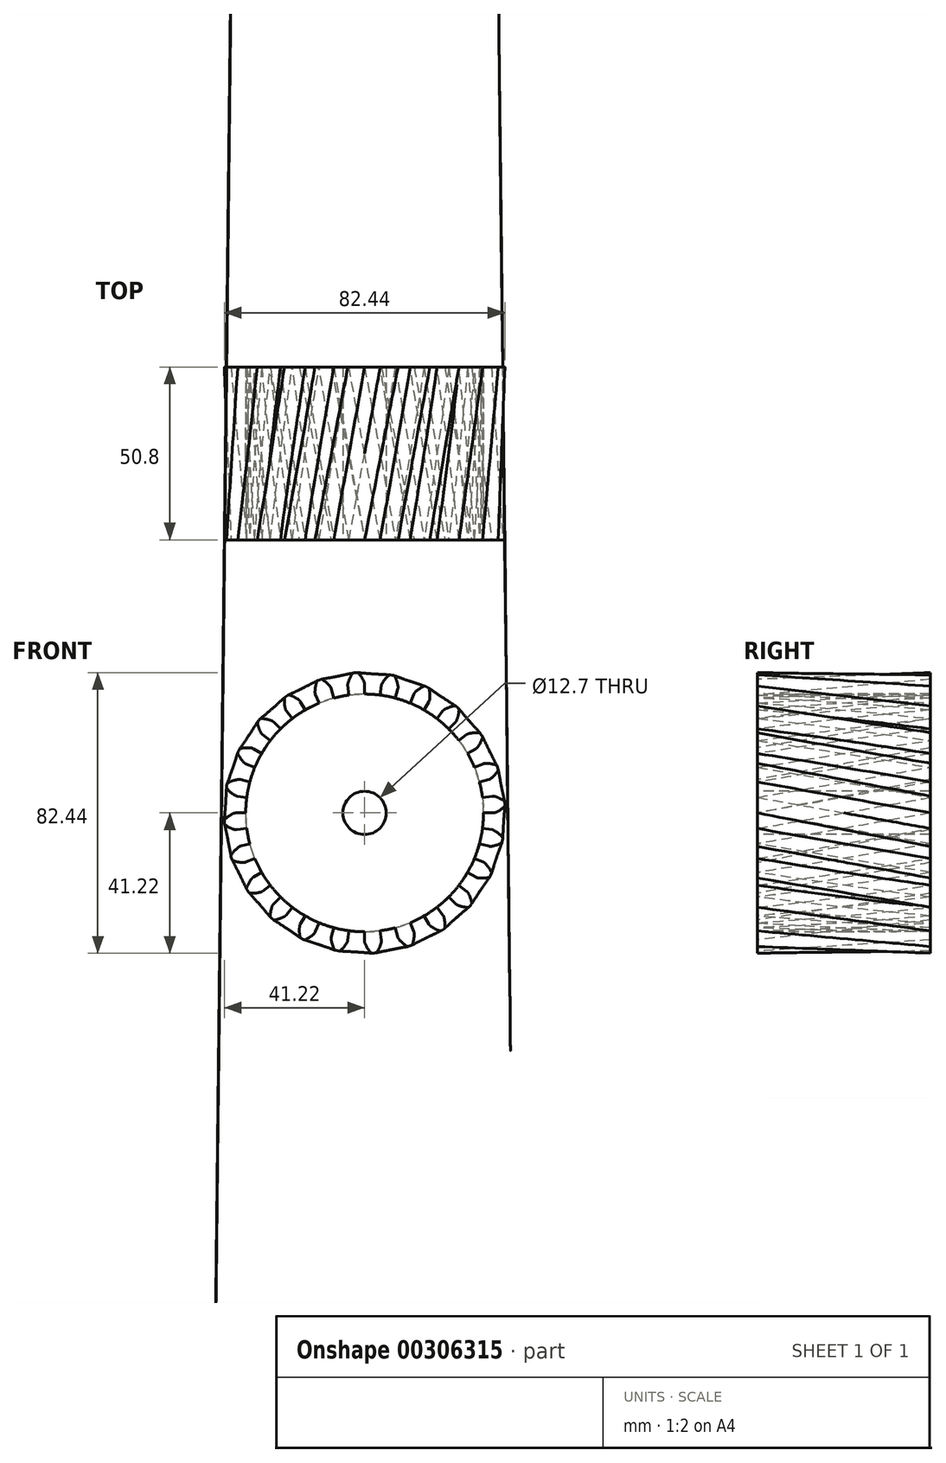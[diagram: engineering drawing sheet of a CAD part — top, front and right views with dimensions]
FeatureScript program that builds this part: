
annotation { "Feature Type Name" : "Feature", "Feature Type Description" : "" }
export const myFeature = defineFeature(function(context is Context, id is Id, definition is map)
    precondition{}
    {
        {
            var Q0;
            Q0=qCreatedBy(makeId("Front.planeOp"),FACE);
            var sketch = newSketch(context, id + "F0", { "sketchPlane" : qUnion([Q0])});
            skCircle(sketch, "E0", {"center": v(0, 0) * mm, "radius": 34.93 * mm});
            skArc(sketch, "E1.trimOffspring", {"start": v(-0.13, 38.41) * mm, "mid": v(-0.86, 39.8) * mm, "end": v(-1.8, 41.05) * mm});
            skLineSegment(sketch, "E2", {"start": v(0, 37.8) * mm, "end": v(0, 34.93) * mm});
            skLineSegment(sketch, "E3", {"start": v(-2.2, 41.22) * mm, "end": v(-2.7, 41.2) * mm});
            skArc(sketch, "E4.MirrorCS", {"start": v(-4.89, 38.1) * mm, "mid": v(-4.34, 39.57) * mm, "end": v(-3.57, 40.93) * mm});
            skLineSegment(sketch, "E5.MirrorCS", {"start": v(-4.93, 37.47) * mm, "end": v(-4.56, 34.63) * mm});
            skLineSegment(sketch, "E6.MirrorCS", {"start": v(-3.2, 41.15) * mm, "end": v(-2.7, 41.2) * mm});
            skPoint(sketch, "E7.visualSharp", {"position": v(-4.97, 37.77) * mm});
            skArc(sketch, "E7.filletArc", {"start": v(-4.89, 38.1) * mm, "mid": v(-4.94, 37.79) * mm, "end": v(-4.93, 37.47) * mm});
            skPoint(sketch, "E8.visualSharp", {"position": v(0, 38.1) * mm});
            skArc(sketch, "E8.filletArc", {"start": v(0, 37.8) * mm, "mid": v(-0.03, 38.1) * mm, "end": v(-0.13, 38.41) * mm});
            skPoint(sketch, "E9.visualSharp", {"position": v(-3.43, 41.13) * mm});
            skArc(sketch, "E9.filletArc", {"start": v(-3.2, 41.15) * mm, "mid": v(-3.4, 41.09) * mm, "end": v(-3.57, 40.93) * mm});
            skPoint(sketch, "E10.visualSharp", {"position": v(-1.97, 41.23) * mm});
            skArc(sketch, "E10.filletArc", {"start": v(-1.8, 41.05) * mm, "mid": v(-1.99, 41.18) * mm, "end": v(-2.2, 41.22) * mm});
            skLineSegment(sketch, "E11.1.0", {"start": v(-14.46, 34.91) * mm, "end": v(-13.37, 32.27) * mm});
            skArc(sketch, "E11.1.1", {"start": v(-14.58, 35.54) * mm, "mid": v(-14.55, 35.22) * mm, "end": v(-14.46, 34.91) * mm});
            skArc(sketch, "E11.1.2", {"start": v(-14.58, 35.54) * mm, "mid": v(-14.44, 37.1) * mm, "end": v(-14.04, 38.62) * mm});
            skLineSegment(sketch, "E11.1.3", {"start": v(-13.73, 38.92) * mm, "end": v(-13.27, 39.1) * mm});
            skLineSegment(sketch, "E11.1.4", {"start": v(-12.8, 39.24) * mm, "end": v(-13.27, 39.1) * mm});
            skArc(sketch, "E11.1.5", {"start": v(-12.37, 39.18) * mm, "mid": v(-12.58, 39.26) * mm, "end": v(-12.8, 39.24) * mm});
            skArc(sketch, "E11.1.6", {"start": v(-10.06, 37.07) * mm, "mid": v(-11.13, 38.22) * mm, "end": v(-12.37, 39.18) * mm});
            skArc(sketch, "E11.1.7", {"start": v(-13.73, 38.92) * mm, "mid": v(-13.92, 38.8) * mm, "end": v(-14.04, 38.62) * mm});
            skArc(sketch, "E11.1.8", {"start": v(-9.78, 36.5) * mm, "mid": v(-9.9, 36.8) * mm, "end": v(-10.06, 37.07) * mm});
            skLineSegment(sketch, "E11.1.9", {"start": v(-9.78, 36.5) * mm, "end": v(-9.04, 33.73) * mm});
            skLineSegment(sketch, "E11.2.0", {"start": v(-23, 29.98) * mm, "end": v(-21.26, 27.7) * mm});
            skArc(sketch, "E11.2.1", {"start": v(-23.28, 30.55) * mm, "mid": v(-23.17, 30.25) * mm, "end": v(-23, 29.98) * mm});
            skArc(sketch, "E11.2.2", {"start": v(-23.28, 30.55) * mm, "mid": v(-23.55, 32.1) * mm, "end": v(-23.56, 33.67) * mm});
            skLineSegment(sketch, "E11.2.3", {"start": v(-23.34, 34.04) * mm, "end": v(-22.93, 34.32) * mm});
            skLineSegment(sketch, "E11.2.4", {"start": v(-22.52, 34.6) * mm, "end": v(-22.93, 34.32) * mm});
            skArc(sketch, "E11.2.5", {"start": v(-22.09, 34.65) * mm, "mid": v(-22.31, 34.67) * mm, "end": v(-22.52, 34.6) * mm});
            skArc(sketch, "E11.2.6", {"start": v(-19.32, 33.2) * mm, "mid": v(-20.64, 34.04) * mm, "end": v(-22.09, 34.65) * mm});
            skArc(sketch, "E11.2.7", {"start": v(-23.34, 34.04) * mm, "mid": v(-23.49, 33.88) * mm, "end": v(-23.56, 33.67) * mm});
            skArc(sketch, "E11.2.8", {"start": v(-18.9, 32.73) * mm, "mid": v(-19.08, 32.99) * mm, "end": v(-19.32, 33.2) * mm});
            skLineSegment(sketch, "E11.2.9", {"start": v(-18.9, 32.73) * mm, "end": v(-17.46, 30.25) * mm});
            skLineSegment(sketch, "E11.3.0", {"start": v(-29.98, 23) * mm, "end": v(-27.7, 21.26) * mm});
            skArc(sketch, "E11.3.1", {"start": v(-30.4, 23.49) * mm, "mid": v(-30.21, 23.22) * mm, "end": v(-29.98, 23) * mm});
            skArc(sketch, "E11.3.2", {"start": v(-30.4, 23.49) * mm, "mid": v(-31.05, 24.9) * mm, "end": v(-31.47, 26.42) * mm});
            skLineSegment(sketch, "E11.3.3", {"start": v(-31.35, 26.84) * mm, "end": v(-31.04, 27.22) * mm});
            skLineSegment(sketch, "E11.3.4", {"start": v(-30.7, 27.58) * mm, "end": v(-31.04, 27.22) * mm});
            skArc(sketch, "E11.3.5", {"start": v(-30.3, 27.75) * mm, "mid": v(-30.52, 27.71) * mm, "end": v(-30.7, 27.58) * mm});
            skArc(sketch, "E11.3.6", {"start": v(-27.25, 27.07) * mm, "mid": v(-28.75, 27.54) * mm, "end": v(-30.3, 27.75) * mm});
            skArc(sketch, "E11.3.7", {"start": v(-31.35, 26.84) * mm, "mid": v(-31.46, 26.65) * mm, "end": v(-31.47, 26.42) * mm});
            skArc(sketch, "E11.3.8", {"start": v(-26.72, 26.72) * mm, "mid": v(-26.97, 26.92) * mm, "end": v(-27.25, 27.07) * mm});
            skLineSegment(sketch, "E11.3.9", {"start": v(-26.72, 26.72) * mm, "end": v(-24.7, 24.7) * mm});
            skLineSegment(sketch, "E11.4.0", {"start": v(-34.91, 14.46) * mm, "end": v(-32.27, 13.37) * mm});
            skArc(sketch, "E11.4.1", {"start": v(-35.44, 14.82) * mm, "mid": v(-35.2, 14.61) * mm, "end": v(-34.91, 14.46) * mm});
            skArc(sketch, "E11.4.2", {"start": v(-35.44, 14.82) * mm, "mid": v(-36.44, 16.02) * mm, "end": v(-37.23, 17.38) * mm});
            skLineSegment(sketch, "E11.4.3", {"start": v(-37.23, 17.81) * mm, "end": v(-37.02, 18.26) * mm});
            skLineSegment(sketch, "E11.4.4", {"start": v(-36.8, 18.7) * mm, "end": v(-37.02, 18.26) * mm});
            skArc(sketch, "E11.4.5", {"start": v(-36.45, 18.96) * mm, "mid": v(-36.66, 18.87) * mm, "end": v(-36.8, 18.7) * mm});
            skArc(sketch, "E11.4.6", {"start": v(-33.33, 19.1) * mm, "mid": v(-34.9, 19.16) * mm, "end": v(-36.45, 18.96) * mm});
            skArc(sketch, "E11.4.7", {"start": v(-37.23, 17.81) * mm, "mid": v(-37.28, 17.6) * mm, "end": v(-37.23, 17.38) * mm});
            skArc(sketch, "E11.4.8", {"start": v(-32.73, 18.9) * mm, "mid": v(-33.02, 19.03) * mm, "end": v(-33.33, 19.1) * mm});
            skLineSegment(sketch, "E11.4.9", {"start": v(-32.73, 18.9) * mm, "end": v(-30.25, 17.46) * mm});
            skLineSegment(sketch, "E11.5.0", {"start": v(-37.47, 4.93) * mm, "end": v(-34.63, 4.56) * mm});
            skArc(sketch, "E11.5.1", {"start": v(-38.07, 5.14) * mm, "mid": v(-37.78, 5) * mm, "end": v(-37.47, 4.93) * mm});
            skArc(sketch, "E11.5.2", {"start": v(-38.07, 5.14) * mm, "mid": v(-39.35, 6.05) * mm, "end": v(-40.46, 7.15) * mm});
            skLineSegment(sketch, "E11.5.3", {"start": v(-40.58, 7.57) * mm, "end": v(-40.49, 8.05) * mm});
            skLineSegment(sketch, "E11.5.4", {"start": v(-40.38, 8.53) * mm, "end": v(-40.49, 8.05) * mm});
            skArc(sketch, "E11.5.5", {"start": v(-40.12, 8.88) * mm, "mid": v(-40.29, 8.74) * mm, "end": v(-40.38, 8.53) * mm});
            skArc(sketch, "E11.5.6", {"start": v(-37.14, 9.82) * mm, "mid": v(-38.67, 9.47) * mm, "end": v(-40.12, 8.88) * mm});
            skArc(sketch, "E11.5.7", {"start": v(-40.58, 7.57) * mm, "mid": v(-40.57, 7.35) * mm, "end": v(-40.46, 7.15) * mm});
            skArc(sketch, "E11.5.8", {"start": v(-36.5, 9.78) * mm, "mid": v(-36.82, 9.83) * mm, "end": v(-37.14, 9.82) * mm});
            skLineSegment(sketch, "E11.5.9", {"start": v(-36.5, 9.78) * mm, "end": v(-33.73, 9.04) * mm});
            skLineSegment(sketch, "E11.6.0", {"start": v(-37.47, -4.93) * mm, "end": v(-34.63, -4.56) * mm});
            skArc(sketch, "E11.6.1", {"start": v(-38.1, -4.89) * mm, "mid": v(-37.79, -4.94) * mm, "end": v(-37.47, -4.93) * mm});
            skArc(sketch, "E11.6.2", {"start": v(-38.1, -4.89) * mm, "mid": v(-39.57, -4.34) * mm, "end": v(-40.93, -3.57) * mm});
            skLineSegment(sketch, "E11.6.3", {"start": v(-41.15, -3.2) * mm, "end": v(-41.2, -2.7) * mm});
            skLineSegment(sketch, "E11.6.4", {"start": v(-41.22, -2.2) * mm, "end": v(-41.2, -2.7) * mm});
            skArc(sketch, "E11.6.5", {"start": v(-41.05, -1.8) * mm, "mid": v(-41.18, -1.99) * mm, "end": v(-41.22, -2.2) * mm});
            skArc(sketch, "E11.6.6", {"start": v(-38.41, -0.13) * mm, "mid": v(-39.8, -0.86) * mm, "end": v(-41.05, -1.8) * mm});
            skArc(sketch, "E11.6.7", {"start": v(-41.15, -3.2) * mm, "mid": v(-41.09, -3.4) * mm, "end": v(-40.93, -3.57) * mm});
            skArc(sketch, "E11.6.8", {"start": v(-37.8, 0) * mm, "mid": v(-38.1, -0.03) * mm, "end": v(-38.41, -0.13) * mm});
            skLineSegment(sketch, "E11.6.9", {"start": v(-37.8, 0) * mm, "end": v(-34.93, 0) * mm});
            skLineSegment(sketch, "E11.7.0", {"start": v(-34.91, -14.46) * mm, "end": v(-32.27, -13.37) * mm});
            skArc(sketch, "E11.7.1", {"start": v(-35.54, -14.58) * mm, "mid": v(-35.22, -14.55) * mm, "end": v(-34.91, -14.46) * mm});
            skArc(sketch, "E11.7.2", {"start": v(-35.54, -14.58) * mm, "mid": v(-37.1, -14.44) * mm, "end": v(-38.62, -14.04) * mm});
            skLineSegment(sketch, "E11.7.3", {"start": v(-38.92, -13.73) * mm, "end": v(-39.1, -13.27) * mm});
            skLineSegment(sketch, "E11.7.4", {"start": v(-39.24, -12.8) * mm, "end": v(-39.1, -13.27) * mm});
            skArc(sketch, "E11.7.5", {"start": v(-39.18, -12.37) * mm, "mid": v(-39.26, -12.58) * mm, "end": v(-39.24, -12.8) * mm});
            skArc(sketch, "E11.7.6", {"start": v(-37.07, -10.06) * mm, "mid": v(-38.22, -11.13) * mm, "end": v(-39.18, -12.37) * mm});
            skArc(sketch, "E11.7.7", {"start": v(-38.92, -13.73) * mm, "mid": v(-38.8, -13.92) * mm, "end": v(-38.62, -14.04) * mm});
            skArc(sketch, "E11.7.8", {"start": v(-36.5, -9.78) * mm, "mid": v(-36.8, -9.9) * mm, "end": v(-37.07, -10.06) * mm});
            skLineSegment(sketch, "E11.7.9", {"start": v(-36.5, -9.78) * mm, "end": v(-33.73, -9.04) * mm});
            skLineSegment(sketch, "E11.8.0", {"start": v(-29.98, -23) * mm, "end": v(-27.7, -21.26) * mm});
            skArc(sketch, "E11.8.1", {"start": v(-30.55, -23.28) * mm, "mid": v(-30.25, -23.17) * mm, "end": v(-29.98, -23) * mm});
            skArc(sketch, "E11.8.2", {"start": v(-30.55, -23.28) * mm, "mid": v(-32.1, -23.55) * mm, "end": v(-33.67, -23.56) * mm});
            skLineSegment(sketch, "E11.8.3", {"start": v(-34.04, -23.34) * mm, "end": v(-34.32, -22.93) * mm});
            skLineSegment(sketch, "E11.8.4", {"start": v(-34.6, -22.52) * mm, "end": v(-34.32, -22.93) * mm});
            skArc(sketch, "E11.8.5", {"start": v(-34.65, -22.09) * mm, "mid": v(-34.67, -22.31) * mm, "end": v(-34.6, -22.52) * mm});
            skArc(sketch, "E11.8.6", {"start": v(-33.2, -19.32) * mm, "mid": v(-34.04, -20.64) * mm, "end": v(-34.65, -22.09) * mm});
            skArc(sketch, "E11.8.7", {"start": v(-34.04, -23.34) * mm, "mid": v(-33.88, -23.49) * mm, "end": v(-33.67, -23.56) * mm});
            skArc(sketch, "E11.8.8", {"start": v(-32.73, -18.9) * mm, "mid": v(-32.99, -19.08) * mm, "end": v(-33.2, -19.32) * mm});
            skLineSegment(sketch, "E11.8.9", {"start": v(-32.73, -18.9) * mm, "end": v(-30.25, -17.46) * mm});
            skLineSegment(sketch, "E11.9.0", {"start": v(-23, -29.98) * mm, "end": v(-21.26, -27.7) * mm});
            skArc(sketch, "E11.9.1", {"start": v(-23.49, -30.4) * mm, "mid": v(-23.22, -30.21) * mm, "end": v(-23, -29.98) * mm});
            skArc(sketch, "E11.9.2", {"start": v(-23.49, -30.4) * mm, "mid": v(-24.9, -31.05) * mm, "end": v(-26.42, -31.47) * mm});
            skLineSegment(sketch, "E11.9.3", {"start": v(-26.84, -31.35) * mm, "end": v(-27.22, -31.04) * mm});
            skLineSegment(sketch, "E11.9.4", {"start": v(-27.58, -30.7) * mm, "end": v(-27.22, -31.04) * mm});
            skArc(sketch, "E11.9.5", {"start": v(-27.75, -30.3) * mm, "mid": v(-27.71, -30.52) * mm, "end": v(-27.58, -30.7) * mm});
            skArc(sketch, "E11.9.6", {"start": v(-27.07, -27.25) * mm, "mid": v(-27.54, -28.75) * mm, "end": v(-27.75, -30.3) * mm});
            skArc(sketch, "E11.9.7", {"start": v(-26.84, -31.35) * mm, "mid": v(-26.65, -31.46) * mm, "end": v(-26.42, -31.47) * mm});
            skArc(sketch, "E11.9.8", {"start": v(-26.72, -26.72) * mm, "mid": v(-26.92, -26.97) * mm, "end": v(-27.07, -27.25) * mm});
            skLineSegment(sketch, "E11.9.9", {"start": v(-26.72, -26.72) * mm, "end": v(-24.7, -24.7) * mm});
            skLineSegment(sketch, "E11.10.0", {"start": v(-14.46, -34.91) * mm, "end": v(-13.37, -32.27) * mm});
            skArc(sketch, "E11.10.1", {"start": v(-14.82, -35.44) * mm, "mid": v(-14.61, -35.2) * mm, "end": v(-14.46, -34.91) * mm});
            skArc(sketch, "E11.10.2", {"start": v(-14.82, -35.44) * mm, "mid": v(-16.02, -36.44) * mm, "end": v(-17.38, -37.23) * mm});
            skLineSegment(sketch, "E11.10.3", {"start": v(-17.81, -37.23) * mm, "end": v(-18.26, -37.02) * mm});
            skLineSegment(sketch, "E11.10.4", {"start": v(-18.7, -36.8) * mm, "end": v(-18.26, -37.02) * mm});
            skArc(sketch, "E11.10.5", {"start": v(-18.96, -36.45) * mm, "mid": v(-18.87, -36.66) * mm, "end": v(-18.7, -36.8) * mm});
            skArc(sketch, "E11.10.6", {"start": v(-19.1, -33.33) * mm, "mid": v(-19.16, -34.9) * mm, "end": v(-18.96, -36.45) * mm});
            skArc(sketch, "E11.10.7", {"start": v(-17.81, -37.23) * mm, "mid": v(-17.6, -37.28) * mm, "end": v(-17.38, -37.23) * mm});
            skArc(sketch, "E11.10.8", {"start": v(-18.9, -32.73) * mm, "mid": v(-19.03, -33.02) * mm, "end": v(-19.1, -33.33) * mm});
            skLineSegment(sketch, "E11.10.9", {"start": v(-18.9, -32.73) * mm, "end": v(-17.46, -30.25) * mm});
            skLineSegment(sketch, "E11.11.0", {"start": v(-4.93, -37.47) * mm, "end": v(-4.56, -34.63) * mm});
            skArc(sketch, "E11.11.1", {"start": v(-5.14, -38.07) * mm, "mid": v(-5, -37.78) * mm, "end": v(-4.93, -37.47) * mm});
            skArc(sketch, "E11.11.2", {"start": v(-5.14, -38.07) * mm, "mid": v(-6.05, -39.35) * mm, "end": v(-7.15, -40.46) * mm});
            skLineSegment(sketch, "E11.11.3", {"start": v(-7.57, -40.58) * mm, "end": v(-8.05, -40.49) * mm});
            skLineSegment(sketch, "E11.11.4", {"start": v(-8.53, -40.38) * mm, "end": v(-8.05, -40.49) * mm});
            skArc(sketch, "E11.11.5", {"start": v(-8.88, -40.12) * mm, "mid": v(-8.74, -40.29) * mm, "end": v(-8.53, -40.38) * mm});
            skArc(sketch, "E11.11.6", {"start": v(-9.82, -37.14) * mm, "mid": v(-9.47, -38.67) * mm, "end": v(-8.88, -40.12) * mm});
            skArc(sketch, "E11.11.7", {"start": v(-7.57, -40.58) * mm, "mid": v(-7.35, -40.57) * mm, "end": v(-7.15, -40.46) * mm});
            skArc(sketch, "E11.11.8", {"start": v(-9.78, -36.5) * mm, "mid": v(-9.83, -36.82) * mm, "end": v(-9.82, -37.14) * mm});
            skLineSegment(sketch, "E11.11.9", {"start": v(-9.78, -36.5) * mm, "end": v(-9.04, -33.73) * mm});
            skLineSegment(sketch, "E11.12.0", {"start": v(4.93, -37.47) * mm, "end": v(4.56, -34.63) * mm});
            skArc(sketch, "E11.12.1", {"start": v(4.89, -38.1) * mm, "mid": v(4.94, -37.79) * mm, "end": v(4.93, -37.47) * mm});
            skArc(sketch, "E11.12.2", {"start": v(4.89, -38.1) * mm, "mid": v(4.34, -39.57) * mm, "end": v(3.57, -40.93) * mm});
            skLineSegment(sketch, "E11.12.3", {"start": v(3.2, -41.15) * mm, "end": v(2.7, -41.2) * mm});
            skLineSegment(sketch, "E11.12.4", {"start": v(2.2, -41.22) * mm, "end": v(2.7, -41.2) * mm});
            skArc(sketch, "E11.12.5", {"start": v(1.8, -41.05) * mm, "mid": v(1.99, -41.18) * mm, "end": v(2.2, -41.22) * mm});
            skArc(sketch, "E11.12.6", {"start": v(0.13, -38.41) * mm, "mid": v(0.86, -39.8) * mm, "end": v(1.8, -41.05) * mm});
            skArc(sketch, "E11.12.7", {"start": v(3.2, -41.15) * mm, "mid": v(3.4, -41.09) * mm, "end": v(3.57, -40.93) * mm});
            skArc(sketch, "E11.12.8", {"start": v(0, -37.8) * mm, "mid": v(0.03, -38.1) * mm, "end": v(0.13, -38.41) * mm});
            skLineSegment(sketch, "E11.12.9", {"start": v(0, -37.8) * mm, "end": v(0, -34.93) * mm});
            skLineSegment(sketch, "E11.13.0", {"start": v(14.46, -34.91) * mm, "end": v(13.37, -32.27) * mm});
            skArc(sketch, "E11.13.1", {"start": v(14.58, -35.54) * mm, "mid": v(14.55, -35.22) * mm, "end": v(14.46, -34.91) * mm});
            skArc(sketch, "E11.13.2", {"start": v(14.58, -35.54) * mm, "mid": v(14.44, -37.1) * mm, "end": v(14.04, -38.62) * mm});
            skLineSegment(sketch, "E11.13.3", {"start": v(13.73, -38.92) * mm, "end": v(13.27, -39.1) * mm});
            skLineSegment(sketch, "E11.13.4", {"start": v(12.8, -39.24) * mm, "end": v(13.27, -39.1) * mm});
            skArc(sketch, "E11.13.5", {"start": v(12.37, -39.18) * mm, "mid": v(12.58, -39.26) * mm, "end": v(12.8, -39.24) * mm});
            skArc(sketch, "E11.13.6", {"start": v(10.06, -37.07) * mm, "mid": v(11.13, -38.22) * mm, "end": v(12.37, -39.18) * mm});
            skArc(sketch, "E11.13.7", {"start": v(13.73, -38.92) * mm, "mid": v(13.92, -38.8) * mm, "end": v(14.04, -38.62) * mm});
            skArc(sketch, "E11.13.8", {"start": v(9.78, -36.5) * mm, "mid": v(9.9, -36.8) * mm, "end": v(10.06, -37.07) * mm});
            skLineSegment(sketch, "E11.13.9", {"start": v(9.78, -36.5) * mm, "end": v(9.04, -33.73) * mm});
            skLineSegment(sketch, "E11.14.0", {"start": v(23, -29.98) * mm, "end": v(21.26, -27.7) * mm});
            skArc(sketch, "E11.14.1", {"start": v(23.28, -30.55) * mm, "mid": v(23.17, -30.25) * mm, "end": v(23, -29.98) * mm});
            skArc(sketch, "E11.14.2", {"start": v(23.28, -30.55) * mm, "mid": v(23.55, -32.1) * mm, "end": v(23.56, -33.67) * mm});
            skLineSegment(sketch, "E11.14.3", {"start": v(23.34, -34.04) * mm, "end": v(22.93, -34.32) * mm});
            skLineSegment(sketch, "E11.14.4", {"start": v(22.52, -34.6) * mm, "end": v(22.93, -34.32) * mm});
            skArc(sketch, "E11.14.5", {"start": v(22.09, -34.65) * mm, "mid": v(22.31, -34.67) * mm, "end": v(22.52, -34.6) * mm});
            skArc(sketch, "E11.14.6", {"start": v(19.32, -33.2) * mm, "mid": v(20.64, -34.04) * mm, "end": v(22.09, -34.65) * mm});
            skArc(sketch, "E11.14.7", {"start": v(23.34, -34.04) * mm, "mid": v(23.49, -33.88) * mm, "end": v(23.56, -33.67) * mm});
            skArc(sketch, "E11.14.8", {"start": v(18.9, -32.73) * mm, "mid": v(19.08, -32.99) * mm, "end": v(19.32, -33.2) * mm});
            skLineSegment(sketch, "E11.14.9", {"start": v(18.9, -32.73) * mm, "end": v(17.46, -30.25) * mm});
            skLineSegment(sketch, "E11.15.0", {"start": v(29.98, -23) * mm, "end": v(27.7, -21.26) * mm});
            skArc(sketch, "E11.15.1", {"start": v(30.4, -23.49) * mm, "mid": v(30.21, -23.22) * mm, "end": v(29.98, -23) * mm});
            skArc(sketch, "E11.15.2", {"start": v(30.4, -23.49) * mm, "mid": v(31.05, -24.9) * mm, "end": v(31.47, -26.42) * mm});
            skLineSegment(sketch, "E11.15.3", {"start": v(31.35, -26.84) * mm, "end": v(31.04, -27.22) * mm});
            skLineSegment(sketch, "E11.15.4", {"start": v(30.7, -27.58) * mm, "end": v(31.04, -27.22) * mm});
            skArc(sketch, "E11.15.5", {"start": v(30.3, -27.75) * mm, "mid": v(30.52, -27.71) * mm, "end": v(30.7, -27.58) * mm});
            skArc(sketch, "E11.15.6", {"start": v(27.25, -27.07) * mm, "mid": v(28.75, -27.54) * mm, "end": v(30.3, -27.75) * mm});
            skArc(sketch, "E11.15.7", {"start": v(31.35, -26.84) * mm, "mid": v(31.46, -26.65) * mm, "end": v(31.47, -26.42) * mm});
            skArc(sketch, "E11.15.8", {"start": v(26.72, -26.72) * mm, "mid": v(26.97, -26.92) * mm, "end": v(27.25, -27.07) * mm});
            skLineSegment(sketch, "E11.15.9", {"start": v(26.72, -26.72) * mm, "end": v(24.7, -24.7) * mm});
            skLineSegment(sketch, "E11.16.0", {"start": v(34.91, -14.46) * mm, "end": v(32.27, -13.37) * mm});
            skArc(sketch, "E11.16.1", {"start": v(35.44, -14.82) * mm, "mid": v(35.2, -14.61) * mm, "end": v(34.91, -14.46) * mm});
            skArc(sketch, "E11.16.2", {"start": v(35.44, -14.82) * mm, "mid": v(36.44, -16.02) * mm, "end": v(37.23, -17.38) * mm});
            skLineSegment(sketch, "E11.16.3", {"start": v(37.23, -17.81) * mm, "end": v(37.02, -18.26) * mm});
            skLineSegment(sketch, "E11.16.4", {"start": v(36.8, -18.7) * mm, "end": v(37.02, -18.26) * mm});
            skArc(sketch, "E11.16.5", {"start": v(36.45, -18.96) * mm, "mid": v(36.66, -18.87) * mm, "end": v(36.8, -18.7) * mm});
            skArc(sketch, "E11.16.6", {"start": v(33.33, -19.1) * mm, "mid": v(34.9, -19.16) * mm, "end": v(36.45, -18.96) * mm});
            skArc(sketch, "E11.16.7", {"start": v(37.23, -17.81) * mm, "mid": v(37.28, -17.6) * mm, "end": v(37.23, -17.38) * mm});
            skArc(sketch, "E11.16.8", {"start": v(32.73, -18.9) * mm, "mid": v(33.02, -19.03) * mm, "end": v(33.33, -19.1) * mm});
            skLineSegment(sketch, "E11.16.9", {"start": v(32.73, -18.9) * mm, "end": v(30.25, -17.46) * mm});
            skLineSegment(sketch, "E11.17.0", {"start": v(37.47, -4.93) * mm, "end": v(34.63, -4.56) * mm});
            skArc(sketch, "E11.17.1", {"start": v(38.07, -5.14) * mm, "mid": v(37.78, -5) * mm, "end": v(37.47, -4.93) * mm});
            skArc(sketch, "E11.17.2", {"start": v(38.07, -5.14) * mm, "mid": v(39.35, -6.05) * mm, "end": v(40.46, -7.15) * mm});
            skLineSegment(sketch, "E11.17.3", {"start": v(40.58, -7.57) * mm, "end": v(40.49, -8.05) * mm});
            skLineSegment(sketch, "E11.17.4", {"start": v(40.38, -8.53) * mm, "end": v(40.49, -8.05) * mm});
            skArc(sketch, "E11.17.5", {"start": v(40.12, -8.88) * mm, "mid": v(40.29, -8.74) * mm, "end": v(40.38, -8.53) * mm});
            skArc(sketch, "E11.17.6", {"start": v(37.14, -9.82) * mm, "mid": v(38.67, -9.47) * mm, "end": v(40.12, -8.88) * mm});
            skArc(sketch, "E11.17.7", {"start": v(40.58, -7.57) * mm, "mid": v(40.57, -7.35) * mm, "end": v(40.46, -7.15) * mm});
            skArc(sketch, "E11.17.8", {"start": v(36.5, -9.78) * mm, "mid": v(36.82, -9.83) * mm, "end": v(37.14, -9.82) * mm});
            skLineSegment(sketch, "E11.17.9", {"start": v(36.5, -9.78) * mm, "end": v(33.73, -9.04) * mm});
            skLineSegment(sketch, "E11.18.0", {"start": v(37.47, 4.93) * mm, "end": v(34.63, 4.56) * mm});
            skArc(sketch, "E11.18.1", {"start": v(38.1, 4.89) * mm, "mid": v(37.79, 4.94) * mm, "end": v(37.47, 4.93) * mm});
            skArc(sketch, "E11.18.2", {"start": v(38.1, 4.89) * mm, "mid": v(39.57, 4.34) * mm, "end": v(40.93, 3.57) * mm});
            skLineSegment(sketch, "E11.18.3", {"start": v(41.15, 3.2) * mm, "end": v(41.2, 2.7) * mm});
            skLineSegment(sketch, "E11.18.4", {"start": v(41.22, 2.2) * mm, "end": v(41.2, 2.7) * mm});
            skArc(sketch, "E11.18.5", {"start": v(41.05, 1.8) * mm, "mid": v(41.18, 1.99) * mm, "end": v(41.22, 2.2) * mm});
            skArc(sketch, "E11.18.6", {"start": v(38.41, 0.13) * mm, "mid": v(39.8, 0.86) * mm, "end": v(41.05, 1.8) * mm});
            skArc(sketch, "E11.18.7", {"start": v(41.15, 3.2) * mm, "mid": v(41.09, 3.4) * mm, "end": v(40.93, 3.57) * mm});
            skArc(sketch, "E11.18.8", {"start": v(37.8, 0) * mm, "mid": v(38.1, 0.03) * mm, "end": v(38.41, 0.13) * mm});
            skLineSegment(sketch, "E11.18.9", {"start": v(37.8, 0) * mm, "end": v(34.93, 0) * mm});
            skLineSegment(sketch, "E11.19.0", {"start": v(34.91, 14.46) * mm, "end": v(32.27, 13.37) * mm});
            skArc(sketch, "E11.19.1", {"start": v(35.54, 14.58) * mm, "mid": v(35.22, 14.55) * mm, "end": v(34.91, 14.46) * mm});
            skArc(sketch, "E11.19.2", {"start": v(35.54, 14.58) * mm, "mid": v(37.1, 14.44) * mm, "end": v(38.62, 14.04) * mm});
            skLineSegment(sketch, "E11.19.3", {"start": v(38.92, 13.73) * mm, "end": v(39.1, 13.27) * mm});
            skLineSegment(sketch, "E11.19.4", {"start": v(39.24, 12.8) * mm, "end": v(39.1, 13.27) * mm});
            skArc(sketch, "E11.19.5", {"start": v(39.18, 12.37) * mm, "mid": v(39.26, 12.58) * mm, "end": v(39.24, 12.8) * mm});
            skArc(sketch, "E11.19.6", {"start": v(37.07, 10.06) * mm, "mid": v(38.22, 11.13) * mm, "end": v(39.18, 12.37) * mm});
            skArc(sketch, "E11.19.7", {"start": v(38.92, 13.73) * mm, "mid": v(38.8, 13.92) * mm, "end": v(38.62, 14.04) * mm});
            skArc(sketch, "E11.19.8", {"start": v(36.5, 9.78) * mm, "mid": v(36.8, 9.9) * mm, "end": v(37.07, 10.06) * mm});
            skLineSegment(sketch, "E11.19.9", {"start": v(36.5, 9.78) * mm, "end": v(33.73, 9.04) * mm});
            skLineSegment(sketch, "E11.20.0", {"start": v(29.98, 23) * mm, "end": v(27.7, 21.26) * mm});
            skArc(sketch, "E11.20.1", {"start": v(30.55, 23.28) * mm, "mid": v(30.25, 23.17) * mm, "end": v(29.98, 23) * mm});
            skArc(sketch, "E11.20.2", {"start": v(30.55, 23.28) * mm, "mid": v(32.1, 23.55) * mm, "end": v(33.67, 23.56) * mm});
            skLineSegment(sketch, "E11.20.3", {"start": v(34.04, 23.34) * mm, "end": v(34.32, 22.93) * mm});
            skLineSegment(sketch, "E11.20.4", {"start": v(34.6, 22.52) * mm, "end": v(34.32, 22.93) * mm});
            skArc(sketch, "E11.20.5", {"start": v(34.65, 22.09) * mm, "mid": v(34.67, 22.31) * mm, "end": v(34.6, 22.52) * mm});
            skArc(sketch, "E11.20.6", {"start": v(33.2, 19.32) * mm, "mid": v(34.04, 20.64) * mm, "end": v(34.65, 22.09) * mm});
            skArc(sketch, "E11.20.7", {"start": v(34.04, 23.34) * mm, "mid": v(33.88, 23.49) * mm, "end": v(33.67, 23.56) * mm});
            skArc(sketch, "E11.20.8", {"start": v(32.73, 18.9) * mm, "mid": v(32.99, 19.08) * mm, "end": v(33.2, 19.32) * mm});
            skLineSegment(sketch, "E11.20.9", {"start": v(32.73, 18.9) * mm, "end": v(30.25, 17.46) * mm});
            skLineSegment(sketch, "E11.21.0", {"start": v(23, 29.98) * mm, "end": v(21.26, 27.7) * mm});
            skArc(sketch, "E11.21.1", {"start": v(23.49, 30.4) * mm, "mid": v(23.22, 30.21) * mm, "end": v(23, 29.98) * mm});
            skArc(sketch, "E11.21.2", {"start": v(23.49, 30.4) * mm, "mid": v(24.9, 31.05) * mm, "end": v(26.42, 31.47) * mm});
            skLineSegment(sketch, "E11.21.3", {"start": v(26.84, 31.35) * mm, "end": v(27.22, 31.04) * mm});
            skLineSegment(sketch, "E11.21.4", {"start": v(27.58, 30.7) * mm, "end": v(27.22, 31.04) * mm});
            skArc(sketch, "E11.21.5", {"start": v(27.75, 30.3) * mm, "mid": v(27.71, 30.52) * mm, "end": v(27.58, 30.7) * mm});
            skArc(sketch, "E11.21.6", {"start": v(27.07, 27.25) * mm, "mid": v(27.54, 28.75) * mm, "end": v(27.75, 30.3) * mm});
            skArc(sketch, "E11.21.7", {"start": v(26.84, 31.35) * mm, "mid": v(26.65, 31.46) * mm, "end": v(26.42, 31.47) * mm});
            skArc(sketch, "E11.21.8", {"start": v(26.72, 26.72) * mm, "mid": v(26.92, 26.97) * mm, "end": v(27.07, 27.25) * mm});
            skLineSegment(sketch, "E11.21.9", {"start": v(26.72, 26.72) * mm, "end": v(24.7, 24.7) * mm});
            skLineSegment(sketch, "E11.22.0", {"start": v(14.46, 34.91) * mm, "end": v(13.37, 32.27) * mm});
            skArc(sketch, "E11.22.1", {"start": v(14.82, 35.44) * mm, "mid": v(14.61, 35.2) * mm, "end": v(14.46, 34.91) * mm});
            skArc(sketch, "E11.22.2", {"start": v(14.82, 35.44) * mm, "mid": v(16.02, 36.44) * mm, "end": v(17.38, 37.23) * mm});
            skLineSegment(sketch, "E11.22.3", {"start": v(17.81, 37.23) * mm, "end": v(18.26, 37.02) * mm});
            skLineSegment(sketch, "E11.22.4", {"start": v(18.7, 36.8) * mm, "end": v(18.26, 37.02) * mm});
            skArc(sketch, "E11.22.5", {"start": v(18.96, 36.45) * mm, "mid": v(18.87, 36.66) * mm, "end": v(18.7, 36.8) * mm});
            skArc(sketch, "E11.22.6", {"start": v(19.1, 33.33) * mm, "mid": v(19.16, 34.9) * mm, "end": v(18.96, 36.45) * mm});
            skArc(sketch, "E11.22.7", {"start": v(17.81, 37.23) * mm, "mid": v(17.6, 37.28) * mm, "end": v(17.38, 37.23) * mm});
            skArc(sketch, "E11.22.8", {"start": v(18.9, 32.73) * mm, "mid": v(19.03, 33.02) * mm, "end": v(19.1, 33.33) * mm});
            skLineSegment(sketch, "E11.22.9", {"start": v(18.9, 32.73) * mm, "end": v(17.46, 30.25) * mm});
            skLineSegment(sketch, "E11.23.0", {"start": v(4.93, 37.47) * mm, "end": v(4.56, 34.63) * mm});
            skArc(sketch, "E11.23.1", {"start": v(5.14, 38.07) * mm, "mid": v(5, 37.78) * mm, "end": v(4.93, 37.47) * mm});
            skArc(sketch, "E11.23.2", {"start": v(5.14, 38.07) * mm, "mid": v(6.05, 39.35) * mm, "end": v(7.15, 40.46) * mm});
            skLineSegment(sketch, "E11.23.3", {"start": v(7.57, 40.58) * mm, "end": v(8.05, 40.49) * mm});
            skLineSegment(sketch, "E11.23.4", {"start": v(8.53, 40.38) * mm, "end": v(8.05, 40.49) * mm});
            skArc(sketch, "E11.23.5", {"start": v(8.88, 40.12) * mm, "mid": v(8.74, 40.29) * mm, "end": v(8.53, 40.38) * mm});
            skArc(sketch, "E11.23.6", {"start": v(9.82, 37.14) * mm, "mid": v(9.47, 38.67) * mm, "end": v(8.88, 40.12) * mm});
            skArc(sketch, "E11.23.7", {"start": v(7.57, 40.58) * mm, "mid": v(7.35, 40.57) * mm, "end": v(7.15, 40.46) * mm});
            skArc(sketch, "E11.23.8", {"start": v(9.78, 36.5) * mm, "mid": v(9.83, 36.82) * mm, "end": v(9.82, 37.14) * mm});
            skLineSegment(sketch, "E11.23.9", {"start": v(9.78, 36.5) * mm, "end": v(9.04, 33.73) * mm});
            skSolve(sketch);
        }
        {
            var Q0;
            {var subQ0=sQuery(id+"F0.wireOp",EDGE,"E0");var subQ1=makeQuery(id+"F0.imprint","INTERSECT",VERTEX,{"derivedFrom":[subQ0,sQuery(id+"F0.wireOp",EDGE,"E2")]});Q0=makeQuery(id+"F0.imprint","IMPRINT",FACE,{"disambiguationData":[TD([[makeQuery(id+"F0.imprint","IMPRINT",EDGE,{"disambiguationData":[TD([[subQ1,-1.0]])],"derivedFrom":subQ0}),1.0]])]});}
            cPlane(context, id + "F1", {"entities" : qUnion([Q0]), "cplaneType" : CPlaneType.OFFSET, "offset" : 50.8 * mm, "width" : 152.4 * mm, "height" : 152.4 * mm});
        }
        {
            var Q0;
            Q0=qCreatedBy(id+"F1.planeOp",FACE);
            var sketch = newSketch(context, id + "F2", { "sketchPlane" : qUnion([Q0])});
            skArc(sketch, "E12.0.0", {"start": v(34.93, 0) * mm, "mid": v(34.85, 2.28) * mm, "end": v(34.63, 4.56) * mm});
            skArc(sketch, "E12.0.1", {"start": v(34.63, 4.56) * mm, "mid": v(34.25, 6.81) * mm, "end": v(33.73, 9.04) * mm});
            skArc(sketch, "E12.0.2", {"start": v(33.73, 9.04) * mm, "mid": v(33.07, 11.23) * mm, "end": v(32.27, 13.37) * mm});
            skArc(sketch, "E12.0.3", {"start": v(32.27, 13.37) * mm, "mid": v(31.32, 15.45) * mm, "end": v(30.25, 17.46) * mm});
            skArc(sketch, "E12.0.4", {"start": v(30.25, 17.46) * mm, "mid": v(29.04, 19.4) * mm, "end": v(27.7, 21.26) * mm});
            skArc(sketch, "E12.0.5", {"start": v(27.7, 21.26) * mm, "mid": v(26.26, 23.03) * mm, "end": v(24.7, 24.7) * mm});
            skArc(sketch, "E12.0.6", {"start": v(24.7, 24.7) * mm, "mid": v(23.03, 26.26) * mm, "end": v(21.26, 27.7) * mm});
            skArc(sketch, "E12.0.7", {"start": v(21.26, 27.7) * mm, "mid": v(19.4, 29.04) * mm, "end": v(17.46, 30.25) * mm});
            skArc(sketch, "E12.0.8", {"start": v(17.46, 30.25) * mm, "mid": v(15.45, 31.32) * mm, "end": v(13.37, 32.27) * mm});
            skArc(sketch, "E12.0.9", {"start": v(13.37, 32.27) * mm, "mid": v(11.23, 33.07) * mm, "end": v(9.04, 33.73) * mm});
            skArc(sketch, "E12.0.10", {"start": v(9.04, 33.73) * mm, "mid": v(6.81, 34.25) * mm, "end": v(4.56, 34.63) * mm});
            skArc(sketch, "E12.0.11", {"start": v(4.56, 34.63) * mm, "mid": v(2.28, 34.85) * mm, "end": v(0, 34.92) * mm});
            skArc(sketch, "E12.0.12", {"start": v(0, 34.93) * mm, "mid": v(-2.28, 34.85) * mm, "end": v(-4.56, 34.63) * mm});
            skArc(sketch, "E12.0.13", {"start": v(-4.56, 34.63) * mm, "mid": v(-6.81, 34.25) * mm, "end": v(-9.04, 33.73) * mm});
            skArc(sketch, "E12.0.14", {"start": v(-9.04, 33.73) * mm, "mid": v(-11.23, 33.07) * mm, "end": v(-13.37, 32.27) * mm});
            skArc(sketch, "E12.0.15", {"start": v(-13.37, 32.27) * mm, "mid": v(-15.45, 31.32) * mm, "end": v(-17.46, 30.25) * mm});
            skArc(sketch, "E12.0.16", {"start": v(-17.46, 30.25) * mm, "mid": v(-19.4, 29.04) * mm, "end": v(-21.26, 27.7) * mm});
            skArc(sketch, "E12.0.17", {"start": v(-21.26, 27.7) * mm, "mid": v(-23.03, 26.26) * mm, "end": v(-24.7, 24.7) * mm});
            skArc(sketch, "E12.0.18", {"start": v(-24.7, 24.7) * mm, "mid": v(-26.26, 23.03) * mm, "end": v(-27.7, 21.26) * mm});
            skArc(sketch, "E12.0.19", {"start": v(-27.7, 21.26) * mm, "mid": v(-29.04, 19.4) * mm, "end": v(-30.25, 17.46) * mm});
            skArc(sketch, "E12.0.20", {"start": v(-30.25, 17.46) * mm, "mid": v(-31.32, 15.45) * mm, "end": v(-32.27, 13.37) * mm});
            skArc(sketch, "E12.0.21", {"start": v(-32.27, 13.37) * mm, "mid": v(-33.07, 11.23) * mm, "end": v(-33.73, 9.04) * mm});
            skArc(sketch, "E12.0.22", {"start": v(-33.73, 9.04) * mm, "mid": v(-34.25, 6.81) * mm, "end": v(-34.63, 4.56) * mm});
            skArc(sketch, "E12.0.23", {"start": v(-34.63, 4.56) * mm, "mid": v(-34.85, 2.28) * mm, "end": v(-34.92, 0) * mm});
            skArc(sketch, "E12.0.24", {"start": v(-34.93, 0) * mm, "mid": v(-34.85, -2.28) * mm, "end": v(-34.63, -4.56) * mm});
            skArc(sketch, "E12.0.25", {"start": v(-34.63, -4.56) * mm, "mid": v(-34.25, -6.81) * mm, "end": v(-33.73, -9.04) * mm});
            skArc(sketch, "E12.0.26", {"start": v(-33.73, -9.04) * mm, "mid": v(-33.07, -11.23) * mm, "end": v(-32.27, -13.37) * mm});
            skArc(sketch, "E12.0.27", {"start": v(-32.27, -13.37) * mm, "mid": v(-31.32, -15.45) * mm, "end": v(-30.25, -17.46) * mm});
            skArc(sketch, "E12.0.28", {"start": v(-30.25, -17.46) * mm, "mid": v(-29.04, -19.4) * mm, "end": v(-27.7, -21.26) * mm});
            skArc(sketch, "E12.0.29", {"start": v(-27.7, -21.26) * mm, "mid": v(-26.26, -23.03) * mm, "end": v(-24.7, -24.7) * mm});
            skArc(sketch, "E12.0.30", {"start": v(-24.7, -24.7) * mm, "mid": v(-23.03, -26.26) * mm, "end": v(-21.26, -27.7) * mm});
            skArc(sketch, "E12.0.31", {"start": v(-21.26, -27.7) * mm, "mid": v(-19.4, -29.04) * mm, "end": v(-17.46, -30.25) * mm});
            skArc(sketch, "E12.0.32", {"start": v(-17.46, -30.25) * mm, "mid": v(-15.45, -31.32) * mm, "end": v(-13.37, -32.27) * mm});
            skArc(sketch, "E12.0.33", {"start": v(-13.37, -32.27) * mm, "mid": v(-11.23, -33.07) * mm, "end": v(-9.04, -33.73) * mm});
            skArc(sketch, "E12.0.34", {"start": v(-9.04, -33.73) * mm, "mid": v(-6.81, -34.25) * mm, "end": v(-4.56, -34.63) * mm});
            skArc(sketch, "E12.0.35", {"start": v(-4.56, -34.63) * mm, "mid": v(-2.28, -34.85) * mm, "end": v(0, -34.92) * mm});
            skArc(sketch, "E12.0.36", {"start": v(0, -34.93) * mm, "mid": v(2.28, -34.85) * mm, "end": v(4.56, -34.63) * mm});
            skArc(sketch, "E12.0.37", {"start": v(4.56, -34.63) * mm, "mid": v(6.81, -34.25) * mm, "end": v(9.04, -33.73) * mm});
            skArc(sketch, "E12.0.38", {"start": v(9.04, -33.73) * mm, "mid": v(11.23, -33.07) * mm, "end": v(13.37, -32.27) * mm});
            skArc(sketch, "E12.0.39", {"start": v(13.37, -32.27) * mm, "mid": v(15.45, -31.32) * mm, "end": v(17.46, -30.25) * mm});
            skArc(sketch, "E12.0.40", {"start": v(17.46, -30.25) * mm, "mid": v(19.4, -29.04) * mm, "end": v(21.26, -27.7) * mm});
            skArc(sketch, "E12.0.41", {"start": v(21.26, -27.7) * mm, "mid": v(23.03, -26.26) * mm, "end": v(24.7, -24.7) * mm});
            skArc(sketch, "E12.0.42", {"start": v(24.7, -24.7) * mm, "mid": v(26.26, -23.03) * mm, "end": v(27.7, -21.26) * mm});
            skArc(sketch, "E12.0.43", {"start": v(27.7, -21.26) * mm, "mid": v(29.04, -19.4) * mm, "end": v(30.25, -17.46) * mm});
            skArc(sketch, "E12.0.44", {"start": v(30.25, -17.46) * mm, "mid": v(31.32, -15.45) * mm, "end": v(32.27, -13.37) * mm});
            skArc(sketch, "E12.0.45", {"start": v(32.27, -13.37) * mm, "mid": v(33.07, -11.23) * mm, "end": v(33.73, -9.04) * mm});
            skArc(sketch, "E12.0.46", {"start": v(33.73, -9.04) * mm, "mid": v(34.25, -6.81) * mm, "end": v(34.63, -4.56) * mm});
            skArc(sketch, "E12.0.47", {"start": v(34.63, -4.56) * mm, "mid": v(34.85, -2.28) * mm, "end": v(34.92, 0) * mm});
            skArc(sketch, "E13.0.0", {"start": v(-3.57, 40.93) * mm, "mid": v(-4.34, 39.57) * mm, "end": v(-4.89, 38.1) * mm});
            skArc(sketch, "E13.0.1", {"start": v(-4.89, 38.1) * mm, "mid": v(-4.94, 37.79) * mm, "end": v(-4.93, 37.47) * mm});
            skLineSegment(sketch, "E13.0.2", {"start": v(-4.93, 37.47) * mm, "end": v(-4.56, 34.63) * mm});
            skArc(sketch, "E13.0.3", {"start": v(-4.56, 34.63) * mm, "mid": v(-2.28, 34.85) * mm, "end": v(0, 34.92) * mm});
            skLineSegment(sketch, "E13.0.4", {"start": v(0, 34.93) * mm, "end": v(0, 37.8) * mm});
            skArc(sketch, "E13.0.5", {"start": v(0, 37.8) * mm, "mid": v(-0.03, 38.1) * mm, "end": v(-0.13, 38.41) * mm});
            skArc(sketch, "E13.0.6", {"start": v(-0.13, 38.41) * mm, "mid": v(-0.86, 39.8) * mm, "end": v(-1.8, 41.05) * mm});
            skArc(sketch, "E13.0.7", {"start": v(-1.8, 41.05) * mm, "mid": v(-1.99, 41.18) * mm, "end": v(-2.2, 41.22) * mm});
            skLineSegment(sketch, "E13.0.8", {"start": v(-2.2, 41.22) * mm, "end": v(-2.7, 41.2) * mm});
            skLineSegment(sketch, "E13.0.9", {"start": v(-2.7, 41.2) * mm, "end": v(-3.2, 41.15) * mm});
            skArc(sketch, "E13.0.10", {"start": v(-3.2, 41.15) * mm, "mid": v(-3.4, 41.09) * mm, "end": v(-3.57, 40.93) * mm});
            skSolve(sketch);
        }
        {
            var Q0;
            Q0=makeQuery(id+"F2.imprint","IMPRINT",FACE,{"disambiguationData":[TD([[makeQuery(id+"F2.imprint","IMPRINT",EDGE,{"derivedFrom":sQuery(id+"F2.wireOp",EDGE,"E13.0.0")}),1.0]])]});
            var Q1;
            {var subQ0=sQuery(id+"F0.wireOp",EDGE,"E11.23.0");Q1=makeQuery(id+"F0.imprint","IMPRINT",FACE,{"disambiguationData":[TD([[makeQuery(id+"F0.imprint","IMPRINT",EDGE,{"derivedFrom":subQ0}),1.0]])]});}
            loft(context, id + "F3", {"sheetProfilesArray" : [{ "sheetProfileEntities" : qUnion([Q0]) }, { "sheetProfileEntities" : qUnion([Q1]) }]});
        }
        {
            var Q0;
            Q0=qCreatedBy(id+"F1.planeOp",FACE);
            var sketch = newSketch(context, id + "F4", { "sketchPlane" : qUnion([Q0])});
            skCircle(sketch, "E14", {"center": v(0, 0) * mm, "radius": 34.92 * mm});
            skSolve(sketch);
        }
        {
            var Q0;
            Q0=makeQuery(id+"F4.imprint","IMPRINT",FACE,{"disambiguationData":[TD([[makeQuery(id+"F4.imprint","IMPRINT",EDGE,{"derivedFrom":sQuery(id+"F4.wireOp",EDGE,"E14")}),1.0]])]});
            var Q1;
            {var subQ0=sQuery(id+"F0.wireOp",EDGE,"E11.23.0");Q1=makeQuery(id+"F3.opLoft","CAP_FACE",FACE,{"disambiguationData":[OSD([makeQuery(id+"F0.imprint","IMPRINT",FACE,{"disambiguationData":[TD([[makeQuery(id+"F0.imprint","IMPRINT",EDGE,{"derivedFrom":subQ0}),1.0]])]})])],"isStart":true});}
            extrude(context, id + "F5", {"entities" : qUnion([Q0]), "operationType" : NewBodyOperationType.ADD, "endBound" : BoundingType.UP_TO_SURFACE, "oppositeDirection" : true, "endBoundEntityFace" : qUnion([Q1]), "depth" : 25.4 * mm});
        }
        {
            var Q0;
            {var subQ0=sQuery(id+"F0.wireOp",EDGE,"E11.23.0");Q0=makeQuery(id+"F3.opLoft","SWEPT_BODY",BODY,{"disambiguationData":[OSD([makeQuery(id+"F0.imprint","IMPRINT",FACE,{"disambiguationData":[TD([[makeQuery(id+"F0.imprint","IMPRINT",EDGE,{"derivedFrom":subQ0}),1.0]])]}),makeQuery(id+"F2.imprint","IMPRINT",FACE,{"disambiguationData":[TD([[makeQuery(id+"F2.imprint","IMPRINT",EDGE,{"derivedFrom":sQuery(id+"F2.wireOp",EDGE,"E13.0.0")}),1.0]])]})])]});}
            var Q1;
            Q1=makeQuery(id+"F5.opExtrude","SWEPT_FACE",FACE,{"disambiguationData":[OSD([sQuery(id+"F4.wireOp",EDGE,"E14")])]});
            circularPattern(context, id + "F6", {"entities" : qUnion([Q0]), "axis" : qUnion([Q1]), "angle" : 360 * degree, "instanceCount" : 24, "equalSpace" : true});
        }
        {
            var Q0;
            {var subQ0=sQuery(id+"F0.wireOp",EDGE,"E11.23.0");Q0=makeQuery(id+"F3.opLoft","SWEPT_BODY",BODY,{"disambiguationData":[OSD([makeQuery(id+"F0.imprint","IMPRINT",FACE,{"disambiguationData":[TD([[makeQuery(id+"F0.imprint","IMPRINT",EDGE,{"derivedFrom":subQ0}),1.0]])]}),makeQuery(id+"F2.imprint","IMPRINT",FACE,{"disambiguationData":[TD([[makeQuery(id+"F2.imprint","IMPRINT",EDGE,{"derivedFrom":sQuery(id+"F2.wireOp",EDGE,"E13.0.0")}),1.0]])]})])]});}
            var Q1;
            {var subQ0=sQuery(id+"F0.wireOp",EDGE,"E11.23.0");Q1=makeQuery(id+"F6.opPattern","COPY",BODY,{"derivedFrom":makeQuery(id+"F3.opLoft","SWEPT_BODY",BODY,{"disambiguationData":[OSD([makeQuery(id+"F0.imprint","IMPRINT",FACE,{"disambiguationData":[TD([[makeQuery(id+"F0.imprint","IMPRINT",EDGE,{"derivedFrom":subQ0}),1.0]])]}),makeQuery(id+"F2.imprint","IMPRINT",FACE,{"disambiguationData":[TD([[makeQuery(id+"F2.imprint","IMPRINT",EDGE,{"derivedFrom":sQuery(id+"F2.wireOp",EDGE,"E13.0.0")}),1.0]])]})])]}),"instanceName":"23"});}
            var Q2;
            {var subQ0=sQuery(id+"F0.wireOp",EDGE,"E11.23.0");Q2=makeQuery(id+"F6.opPattern","COPY",BODY,{"derivedFrom":makeQuery(id+"F3.opLoft","SWEPT_BODY",BODY,{"disambiguationData":[OSD([makeQuery(id+"F0.imprint","IMPRINT",FACE,{"disambiguationData":[TD([[makeQuery(id+"F0.imprint","IMPRINT",EDGE,{"derivedFrom":subQ0}),1.0]])]}),makeQuery(id+"F2.imprint","IMPRINT",FACE,{"disambiguationData":[TD([[makeQuery(id+"F2.imprint","IMPRINT",EDGE,{"derivedFrom":sQuery(id+"F2.wireOp",EDGE,"E13.0.0")}),1.0]])]})])]}),"instanceName":"22"});}
            var Q3;
            {var subQ0=sQuery(id+"F0.wireOp",EDGE,"E11.23.0");Q3=makeQuery(id+"F6.opPattern","COPY",BODY,{"derivedFrom":makeQuery(id+"F3.opLoft","SWEPT_BODY",BODY,{"disambiguationData":[OSD([makeQuery(id+"F0.imprint","IMPRINT",FACE,{"disambiguationData":[TD([[makeQuery(id+"F0.imprint","IMPRINT",EDGE,{"derivedFrom":subQ0}),1.0]])]}),makeQuery(id+"F2.imprint","IMPRINT",FACE,{"disambiguationData":[TD([[makeQuery(id+"F2.imprint","IMPRINT",EDGE,{"derivedFrom":sQuery(id+"F2.wireOp",EDGE,"E13.0.0")}),1.0]])]})])]}),"instanceName":"21"});}
            var Q4;
            {var subQ0=sQuery(id+"F0.wireOp",EDGE,"E11.23.0");Q4=makeQuery(id+"F6.opPattern","COPY",BODY,{"derivedFrom":makeQuery(id+"F3.opLoft","SWEPT_BODY",BODY,{"disambiguationData":[OSD([makeQuery(id+"F0.imprint","IMPRINT",FACE,{"disambiguationData":[TD([[makeQuery(id+"F0.imprint","IMPRINT",EDGE,{"derivedFrom":subQ0}),1.0]])]}),makeQuery(id+"F2.imprint","IMPRINT",FACE,{"disambiguationData":[TD([[makeQuery(id+"F2.imprint","IMPRINT",EDGE,{"derivedFrom":sQuery(id+"F2.wireOp",EDGE,"E13.0.0")}),1.0]])]})])]}),"instanceName":"20"});}
            var Q5;
            {var subQ0=sQuery(id+"F0.wireOp",EDGE,"E11.23.0");Q5=makeQuery(id+"F6.opPattern","COPY",BODY,{"derivedFrom":makeQuery(id+"F3.opLoft","SWEPT_BODY",BODY,{"disambiguationData":[OSD([makeQuery(id+"F0.imprint","IMPRINT",FACE,{"disambiguationData":[TD([[makeQuery(id+"F0.imprint","IMPRINT",EDGE,{"derivedFrom":subQ0}),1.0]])]}),makeQuery(id+"F2.imprint","IMPRINT",FACE,{"disambiguationData":[TD([[makeQuery(id+"F2.imprint","IMPRINT",EDGE,{"derivedFrom":sQuery(id+"F2.wireOp",EDGE,"E13.0.0")}),1.0]])]})])]}),"instanceName":"19"});}
            var Q6;
            {var subQ0=sQuery(id+"F0.wireOp",EDGE,"E11.23.0");Q6=makeQuery(id+"F6.opPattern","COPY",BODY,{"derivedFrom":makeQuery(id+"F3.opLoft","SWEPT_BODY",BODY,{"disambiguationData":[OSD([makeQuery(id+"F0.imprint","IMPRINT",FACE,{"disambiguationData":[TD([[makeQuery(id+"F0.imprint","IMPRINT",EDGE,{"derivedFrom":subQ0}),1.0]])]}),makeQuery(id+"F2.imprint","IMPRINT",FACE,{"disambiguationData":[TD([[makeQuery(id+"F2.imprint","IMPRINT",EDGE,{"derivedFrom":sQuery(id+"F2.wireOp",EDGE,"E13.0.0")}),1.0]])]})])]}),"instanceName":"18"});}
            var Q7;
            {var subQ0=sQuery(id+"F0.wireOp",EDGE,"E11.23.0");Q7=makeQuery(id+"F6.opPattern","COPY",BODY,{"derivedFrom":makeQuery(id+"F3.opLoft","SWEPT_BODY",BODY,{"disambiguationData":[OSD([makeQuery(id+"F0.imprint","IMPRINT",FACE,{"disambiguationData":[TD([[makeQuery(id+"F0.imprint","IMPRINT",EDGE,{"derivedFrom":subQ0}),1.0]])]}),makeQuery(id+"F2.imprint","IMPRINT",FACE,{"disambiguationData":[TD([[makeQuery(id+"F2.imprint","IMPRINT",EDGE,{"derivedFrom":sQuery(id+"F2.wireOp",EDGE,"E13.0.0")}),1.0]])]})])]}),"instanceName":"17"});}
            var Q8;
            {var subQ0=sQuery(id+"F0.wireOp",EDGE,"E11.23.0");Q8=makeQuery(id+"F6.opPattern","COPY",BODY,{"derivedFrom":makeQuery(id+"F3.opLoft","SWEPT_BODY",BODY,{"disambiguationData":[OSD([makeQuery(id+"F0.imprint","IMPRINT",FACE,{"disambiguationData":[TD([[makeQuery(id+"F0.imprint","IMPRINT",EDGE,{"derivedFrom":subQ0}),1.0]])]}),makeQuery(id+"F2.imprint","IMPRINT",FACE,{"disambiguationData":[TD([[makeQuery(id+"F2.imprint","IMPRINT",EDGE,{"derivedFrom":sQuery(id+"F2.wireOp",EDGE,"E13.0.0")}),1.0]])]})])]}),"instanceName":"16"});}
            var Q9;
            {var subQ0=sQuery(id+"F0.wireOp",EDGE,"E11.23.0");Q9=makeQuery(id+"F6.opPattern","COPY",BODY,{"derivedFrom":makeQuery(id+"F3.opLoft","SWEPT_BODY",BODY,{"disambiguationData":[OSD([makeQuery(id+"F0.imprint","IMPRINT",FACE,{"disambiguationData":[TD([[makeQuery(id+"F0.imprint","IMPRINT",EDGE,{"derivedFrom":subQ0}),1.0]])]}),makeQuery(id+"F2.imprint","IMPRINT",FACE,{"disambiguationData":[TD([[makeQuery(id+"F2.imprint","IMPRINT",EDGE,{"derivedFrom":sQuery(id+"F2.wireOp",EDGE,"E13.0.0")}),1.0]])]})])]}),"instanceName":"15"});}
            var Q10;
            {var subQ0=sQuery(id+"F0.wireOp",EDGE,"E11.23.0");Q10=makeQuery(id+"F6.opPattern","COPY",BODY,{"derivedFrom":makeQuery(id+"F3.opLoft","SWEPT_BODY",BODY,{"disambiguationData":[OSD([makeQuery(id+"F0.imprint","IMPRINT",FACE,{"disambiguationData":[TD([[makeQuery(id+"F0.imprint","IMPRINT",EDGE,{"derivedFrom":subQ0}),1.0]])]}),makeQuery(id+"F2.imprint","IMPRINT",FACE,{"disambiguationData":[TD([[makeQuery(id+"F2.imprint","IMPRINT",EDGE,{"derivedFrom":sQuery(id+"F2.wireOp",EDGE,"E13.0.0")}),1.0]])]})])]}),"instanceName":"14"});}
            var Q11;
            {var subQ0=sQuery(id+"F0.wireOp",EDGE,"E11.23.0");Q11=makeQuery(id+"F6.opPattern","COPY",BODY,{"derivedFrom":makeQuery(id+"F3.opLoft","SWEPT_BODY",BODY,{"disambiguationData":[OSD([makeQuery(id+"F0.imprint","IMPRINT",FACE,{"disambiguationData":[TD([[makeQuery(id+"F0.imprint","IMPRINT",EDGE,{"derivedFrom":subQ0}),1.0]])]}),makeQuery(id+"F2.imprint","IMPRINT",FACE,{"disambiguationData":[TD([[makeQuery(id+"F2.imprint","IMPRINT",EDGE,{"derivedFrom":sQuery(id+"F2.wireOp",EDGE,"E13.0.0")}),1.0]])]})])]}),"instanceName":"13"});}
            var Q12;
            {var subQ0=sQuery(id+"F0.wireOp",EDGE,"E11.23.0");Q12=makeQuery(id+"F6.opPattern","COPY",BODY,{"derivedFrom":makeQuery(id+"F3.opLoft","SWEPT_BODY",BODY,{"disambiguationData":[OSD([makeQuery(id+"F0.imprint","IMPRINT",FACE,{"disambiguationData":[TD([[makeQuery(id+"F0.imprint","IMPRINT",EDGE,{"derivedFrom":subQ0}),1.0]])]}),makeQuery(id+"F2.imprint","IMPRINT",FACE,{"disambiguationData":[TD([[makeQuery(id+"F2.imprint","IMPRINT",EDGE,{"derivedFrom":sQuery(id+"F2.wireOp",EDGE,"E13.0.0")}),1.0]])]})])]}),"instanceName":"12"});}
            var Q13;
            {var subQ0=sQuery(id+"F0.wireOp",EDGE,"E11.23.0");Q13=makeQuery(id+"F6.opPattern","COPY",BODY,{"derivedFrom":makeQuery(id+"F3.opLoft","SWEPT_BODY",BODY,{"disambiguationData":[OSD([makeQuery(id+"F0.imprint","IMPRINT",FACE,{"disambiguationData":[TD([[makeQuery(id+"F0.imprint","IMPRINT",EDGE,{"derivedFrom":subQ0}),1.0]])]}),makeQuery(id+"F2.imprint","IMPRINT",FACE,{"disambiguationData":[TD([[makeQuery(id+"F2.imprint","IMPRINT",EDGE,{"derivedFrom":sQuery(id+"F2.wireOp",EDGE,"E13.0.0")}),1.0]])]})])]}),"instanceName":"11"});}
            var Q14;
            {var subQ0=sQuery(id+"F0.wireOp",EDGE,"E11.23.0");Q14=makeQuery(id+"F6.opPattern","COPY",BODY,{"derivedFrom":makeQuery(id+"F3.opLoft","SWEPT_BODY",BODY,{"disambiguationData":[OSD([makeQuery(id+"F0.imprint","IMPRINT",FACE,{"disambiguationData":[TD([[makeQuery(id+"F0.imprint","IMPRINT",EDGE,{"derivedFrom":subQ0}),1.0]])]}),makeQuery(id+"F2.imprint","IMPRINT",FACE,{"disambiguationData":[TD([[makeQuery(id+"F2.imprint","IMPRINT",EDGE,{"derivedFrom":sQuery(id+"F2.wireOp",EDGE,"E13.0.0")}),1.0]])]})])]}),"instanceName":"10"});}
            var Q15;
            {var subQ0=sQuery(id+"F0.wireOp",EDGE,"E11.23.0");Q15=makeQuery(id+"F6.opPattern","COPY",BODY,{"derivedFrom":makeQuery(id+"F3.opLoft","SWEPT_BODY",BODY,{"disambiguationData":[OSD([makeQuery(id+"F0.imprint","IMPRINT",FACE,{"disambiguationData":[TD([[makeQuery(id+"F0.imprint","IMPRINT",EDGE,{"derivedFrom":subQ0}),1.0]])]}),makeQuery(id+"F2.imprint","IMPRINT",FACE,{"disambiguationData":[TD([[makeQuery(id+"F2.imprint","IMPRINT",EDGE,{"derivedFrom":sQuery(id+"F2.wireOp",EDGE,"E13.0.0")}),1.0]])]})])]}),"instanceName":"9"});}
            var Q16;
            {var subQ0=sQuery(id+"F0.wireOp",EDGE,"E11.23.0");Q16=makeQuery(id+"F6.opPattern","COPY",BODY,{"derivedFrom":makeQuery(id+"F3.opLoft","SWEPT_BODY",BODY,{"disambiguationData":[OSD([makeQuery(id+"F0.imprint","IMPRINT",FACE,{"disambiguationData":[TD([[makeQuery(id+"F0.imprint","IMPRINT",EDGE,{"derivedFrom":subQ0}),1.0]])]}),makeQuery(id+"F2.imprint","IMPRINT",FACE,{"disambiguationData":[TD([[makeQuery(id+"F2.imprint","IMPRINT",EDGE,{"derivedFrom":sQuery(id+"F2.wireOp",EDGE,"E13.0.0")}),1.0]])]})])]}),"instanceName":"8"});}
            var Q17;
            {var subQ0=sQuery(id+"F0.wireOp",EDGE,"E11.23.0");Q17=makeQuery(id+"F6.opPattern","COPY",BODY,{"derivedFrom":makeQuery(id+"F3.opLoft","SWEPT_BODY",BODY,{"disambiguationData":[OSD([makeQuery(id+"F0.imprint","IMPRINT",FACE,{"disambiguationData":[TD([[makeQuery(id+"F0.imprint","IMPRINT",EDGE,{"derivedFrom":subQ0}),1.0]])]}),makeQuery(id+"F2.imprint","IMPRINT",FACE,{"disambiguationData":[TD([[makeQuery(id+"F2.imprint","IMPRINT",EDGE,{"derivedFrom":sQuery(id+"F2.wireOp",EDGE,"E13.0.0")}),1.0]])]})])]}),"instanceName":"7"});}
            var Q18;
            {var subQ0=sQuery(id+"F0.wireOp",EDGE,"E11.23.0");Q18=makeQuery(id+"F6.opPattern","COPY",BODY,{"derivedFrom":makeQuery(id+"F3.opLoft","SWEPT_BODY",BODY,{"disambiguationData":[OSD([makeQuery(id+"F0.imprint","IMPRINT",FACE,{"disambiguationData":[TD([[makeQuery(id+"F0.imprint","IMPRINT",EDGE,{"derivedFrom":subQ0}),1.0]])]}),makeQuery(id+"F2.imprint","IMPRINT",FACE,{"disambiguationData":[TD([[makeQuery(id+"F2.imprint","IMPRINT",EDGE,{"derivedFrom":sQuery(id+"F2.wireOp",EDGE,"E13.0.0")}),1.0]])]})])]}),"instanceName":"6"});}
            var Q19;
            {var subQ0=sQuery(id+"F0.wireOp",EDGE,"E11.23.0");Q19=makeQuery(id+"F6.opPattern","COPY",BODY,{"derivedFrom":makeQuery(id+"F3.opLoft","SWEPT_BODY",BODY,{"disambiguationData":[OSD([makeQuery(id+"F0.imprint","IMPRINT",FACE,{"disambiguationData":[TD([[makeQuery(id+"F0.imprint","IMPRINT",EDGE,{"derivedFrom":subQ0}),1.0]])]}),makeQuery(id+"F2.imprint","IMPRINT",FACE,{"disambiguationData":[TD([[makeQuery(id+"F2.imprint","IMPRINT",EDGE,{"derivedFrom":sQuery(id+"F2.wireOp",EDGE,"E13.0.0")}),1.0]])]})])]}),"instanceName":"5"});}
            var Q20;
            {var subQ0=sQuery(id+"F0.wireOp",EDGE,"E11.23.0");Q20=makeQuery(id+"F6.opPattern","COPY",BODY,{"derivedFrom":makeQuery(id+"F3.opLoft","SWEPT_BODY",BODY,{"disambiguationData":[OSD([makeQuery(id+"F0.imprint","IMPRINT",FACE,{"disambiguationData":[TD([[makeQuery(id+"F0.imprint","IMPRINT",EDGE,{"derivedFrom":subQ0}),1.0]])]}),makeQuery(id+"F2.imprint","IMPRINT",FACE,{"disambiguationData":[TD([[makeQuery(id+"F2.imprint","IMPRINT",EDGE,{"derivedFrom":sQuery(id+"F2.wireOp",EDGE,"E13.0.0")}),1.0]])]})])]}),"instanceName":"4"});}
            var Q21;
            {var subQ0=sQuery(id+"F0.wireOp",EDGE,"E11.23.0");Q21=makeQuery(id+"F6.opPattern","COPY",BODY,{"derivedFrom":makeQuery(id+"F3.opLoft","SWEPT_BODY",BODY,{"disambiguationData":[OSD([makeQuery(id+"F0.imprint","IMPRINT",FACE,{"disambiguationData":[TD([[makeQuery(id+"F0.imprint","IMPRINT",EDGE,{"derivedFrom":subQ0}),1.0]])]}),makeQuery(id+"F2.imprint","IMPRINT",FACE,{"disambiguationData":[TD([[makeQuery(id+"F2.imprint","IMPRINT",EDGE,{"derivedFrom":sQuery(id+"F2.wireOp",EDGE,"E13.0.0")}),1.0]])]})])]}),"instanceName":"3"});}
            var Q22;
            {var subQ0=sQuery(id+"F0.wireOp",EDGE,"E11.23.0");Q22=makeQuery(id+"F6.opPattern","COPY",BODY,{"derivedFrom":makeQuery(id+"F3.opLoft","SWEPT_BODY",BODY,{"disambiguationData":[OSD([makeQuery(id+"F0.imprint","IMPRINT",FACE,{"disambiguationData":[TD([[makeQuery(id+"F0.imprint","IMPRINT",EDGE,{"derivedFrom":subQ0}),1.0]])]}),makeQuery(id+"F2.imprint","IMPRINT",FACE,{"disambiguationData":[TD([[makeQuery(id+"F2.imprint","IMPRINT",EDGE,{"derivedFrom":sQuery(id+"F2.wireOp",EDGE,"E13.0.0")}),1.0]])]})])]}),"instanceName":"2"});}
            var Q23;
            {var subQ0=sQuery(id+"F0.wireOp",EDGE,"E11.23.0");Q23=makeQuery(id+"F6.opPattern","COPY",BODY,{"derivedFrom":makeQuery(id+"F3.opLoft","SWEPT_BODY",BODY,{"disambiguationData":[OSD([makeQuery(id+"F0.imprint","IMPRINT",FACE,{"disambiguationData":[TD([[makeQuery(id+"F0.imprint","IMPRINT",EDGE,{"derivedFrom":subQ0}),1.0]])]}),makeQuery(id+"F2.imprint","IMPRINT",FACE,{"disambiguationData":[TD([[makeQuery(id+"F2.imprint","IMPRINT",EDGE,{"derivedFrom":sQuery(id+"F2.wireOp",EDGE,"E13.0.0")}),1.0]])]})])]}),"instanceName":"1"});}
            booleanBodies(context, id + "F7", {"operationType" : BooleanOperationType.UNION, "tools" : qUnion([Q0, Q1, Q2, Q3, Q4, Q5, Q6, Q7, Q8, Q9, Q10, Q11, Q12, Q13, Q14, Q15, Q16, Q17, Q18, Q19, Q20, Q21, Q22, Q23])});
        }
        {
            var Q0;
            {var subQ0=makeQuery(id+"F5.boolean.opBoolean","MERGE",FACE,{"derivedFrom":[makeQuery(id+"F3.opLoft","CAP_FACE",FACE,{"disambiguationData":[OSD([makeQuery(id+"F2.imprint","IMPRINT",FACE,{"disambiguationData":[TD([[makeQuery(id+"F2.imprint","IMPRINT",EDGE,{"derivedFrom":sQuery(id+"F2.wireOp",EDGE,"E13.0.0")}),1.0]])]})])],"isStart":true}),makeQuery(id+"F5.opExtrude","CAP_FACE",FACE,{"disambiguationData":[OSD([sQuery(id+"F4.wireOp",EDGE,"E14")])],"isStart":true})]});Q0=makeQuery(id+"F7.opBoolean","MERGE",FACE,{"derivedFrom":[subQ0,makeQuery(id+"F6.opPattern","COPY",FACE,{"derivedFrom":subQ0,"instanceName":"1"}),makeQuery(id+"F6.opPattern","COPY",FACE,{"derivedFrom":subQ0,"instanceName":"2"}),makeQuery(id+"F6.opPattern","COPY",FACE,{"derivedFrom":subQ0,"instanceName":"3"}),makeQuery(id+"F6.opPattern","COPY",FACE,{"derivedFrom":subQ0,"instanceName":"4"}),makeQuery(id+"F6.opPattern","COPY",FACE,{"derivedFrom":subQ0,"instanceName":"5"}),makeQuery(id+"F6.opPattern","COPY",FACE,{"derivedFrom":subQ0,"instanceName":"6"}),makeQuery(id+"F6.opPattern","COPY",FACE,{"derivedFrom":subQ0,"instanceName":"7"}),makeQuery(id+"F6.opPattern","COPY",FACE,{"derivedFrom":subQ0,"instanceName":"8"}),makeQuery(id+"F6.opPattern","COPY",FACE,{"derivedFrom":subQ0,"instanceName":"9"}),makeQuery(id+"F6.opPattern","COPY",FACE,{"derivedFrom":subQ0,"instanceName":"10"}),makeQuery(id+"F6.opPattern","COPY",FACE,{"derivedFrom":subQ0,"instanceName":"11"}),makeQuery(id+"F6.opPattern","COPY",FACE,{"derivedFrom":subQ0,"instanceName":"12"}),makeQuery(id+"F6.opPattern","COPY",FACE,{"derivedFrom":subQ0,"instanceName":"13"}),makeQuery(id+"F6.opPattern","COPY",FACE,{"derivedFrom":subQ0,"instanceName":"14"}),makeQuery(id+"F6.opPattern","COPY",FACE,{"derivedFrom":subQ0,"instanceName":"15"}),makeQuery(id+"F6.opPattern","COPY",FACE,{"derivedFrom":subQ0,"instanceName":"16"}),makeQuery(id+"F6.opPattern","COPY",FACE,{"derivedFrom":subQ0,"instanceName":"17"}),makeQuery(id+"F6.opPattern","COPY",FACE,{"derivedFrom":subQ0,"instanceName":"18"}),makeQuery(id+"F6.opPattern","COPY",FACE,{"derivedFrom":subQ0,"instanceName":"19"}),makeQuery(id+"F6.opPattern","COPY",FACE,{"derivedFrom":subQ0,"instanceName":"20"}),makeQuery(id+"F6.opPattern","COPY",FACE,{"derivedFrom":subQ0,"instanceName":"21"}),makeQuery(id+"F6.opPattern","COPY",FACE,{"derivedFrom":subQ0,"instanceName":"22"}),makeQuery(id+"F6.opPattern","COPY",FACE,{"derivedFrom":subQ0,"instanceName":"23"})]});}
            var sketch = newSketch(context, id + "F8", { "sketchPlane" : qUnion([Q0])});
            skCircle(sketch, "E15", {"center": v(0, 0) * mm, "radius": 6.35 * mm});
            skSolve(sketch);
        }
        {
            var Q0;
            Q0 = qSketchRegion(id + "F8", true);
            extrude(context, id + "F9", {"entities" : qUnion([Q0]), "operationType" : NewBodyOperationType.REMOVE, "endBound" : BoundingType.THROUGH_ALL, "oppositeDirection" : true, "depth" : 25.4 * mm});
        }
    });
